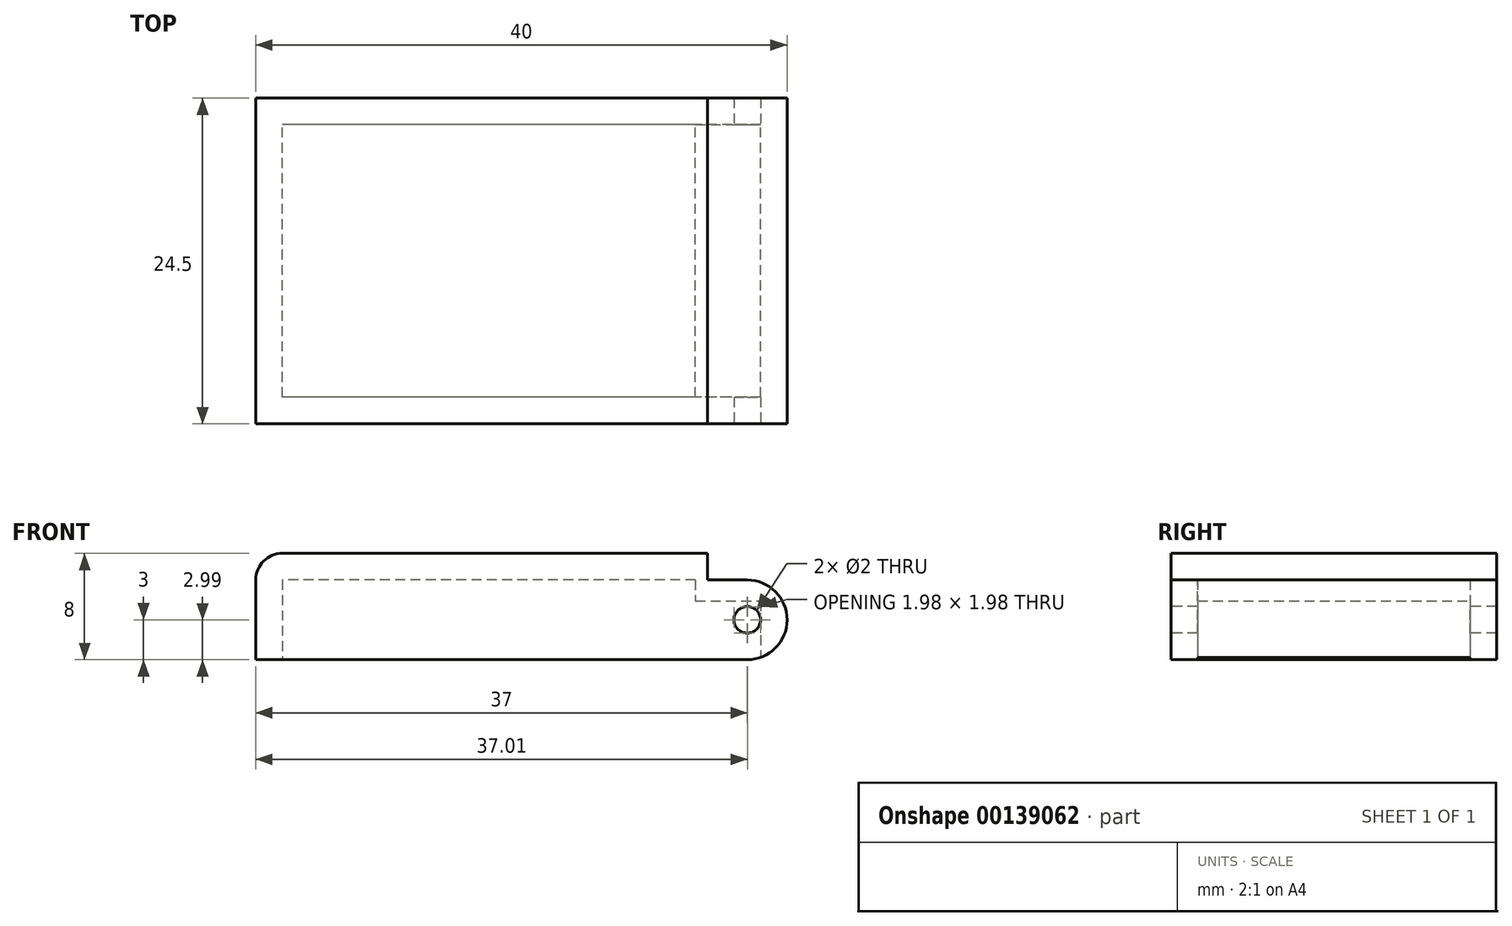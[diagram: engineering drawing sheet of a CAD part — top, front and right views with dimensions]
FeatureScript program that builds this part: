
annotation { "Feature Type Name" : "Feature", "Feature Type Description" : "" }
export const myFeature = defineFeature(function(context is Context, id is Id, definition is map)
    precondition{}
    {
        {
            var Q0;
            Q0=qCreatedBy(makeId("Top.planeOp"),FACE);
            var sketch = newSketch(context, id + "F0", { "sketchPlane" : qUnion([Q0])});
            skLineSegment(sketch, "E0.bottom", {"start": v(20, -12.25) * mm, "end": v(-20, -12.25) * mm});
            skLineSegment(sketch, "E0.top", {"start": v(20, 12.25) * mm, "end": v(-20, 12.25) * mm});
            skLineSegment(sketch, "E0.left", {"start": v(20, -12.25) * mm, "end": v(20, 12.25) * mm});
            skLineSegment(sketch, "E0.right", {"start": v(-20, -12.25) * mm, "end": v(-20, 12.25) * mm});
            skPoint(sketch, "E0.middle", {"position": v(0, 0) * mm});
            skSolve(sketch);
        }
        {
            var Q0;
            Q0 = qSketchRegion(id + "F0", true);
            extrude(context, id + "F1", {"entities" : qUnion([Q0]), "depth" : 8 * mm});
        }
        {
            var Q0;
            Q0=makeQuery(id+"F1.opExtrude","CAP_FACE",FACE,{"disambiguationData":[OSD([sQuery(id+"F0.wireOp",EDGE,"E0.bottom"),sQuery(id+"F0.wireOp",EDGE,"E0.top"),sQuery(id+"F0.wireOp",EDGE,"E0.left"),sQuery(id+"F0.wireOp",EDGE,"E0.right")])],"isStart":true});
            shell(context, id + "F2", {"entities" : qUnion([Q0]), "thickness" : 2 * mm});
        }
        {
            var Q0;
            Q0=makeQuery(id+"F1.opExtrude","SWEPT_FACE",FACE,{"disambiguationData":[OSD([sQuery(id+"F0.wireOp",EDGE,"E0.bottom")])]});
            var sketch = newSketch(context, id + "F3", { "sketchPlane" : qUnion([Q0])});
            skCircle(sketch, "E1", {"center": v(17, 3) * mm, "radius": 1 * mm});
            skArc(sketch, "E2", {"start": v(17, 0) * mm, "mid": v(20, 3) * mm, "end": v(17, 6) * mm});
            skLineSegment(sketch, "E3", {"start": v(17, 3) * mm, "end": v(17, 8) * mm, "construction": true});
            skLineSegment(sketch, "E4", {"start": v(17, 3) * mm, "end": v(0, 3) * mm, "construction": true});
            skLineSegment(sketch, "E5", {"start": v(14, 3) * mm, "end": v(14, 8) * mm, "construction": true});
            skLineSegment(sketch, "E6", {"start": v(17, 6) * mm, "end": v(14, 6) * mm, "construction": true});
            skLineSegment(sketch, "E7", {"start": v(14, 8) * mm, "end": v(14, 6) * mm});
            skLineSegment(sketch, "E8", {"start": v(14, 6) * mm, "end": v(17, 6) * mm});
            skLineSegment(sketch, "E9", {"start": v(17, 0) * mm, "end": v(20, 0) * mm});
            skLineSegment(sketch, "E10", {"start": v(20, 0) * mm, "end": v(20, 3) * mm});
            skLineSegment(sketch, "E11", {"start": v(14, 8) * mm, "end": v(20, 8) * mm});
            skLineSegment(sketch, "E12", {"start": v(20, 8) * mm, "end": v(20, 3) * mm});
            skSolve(sketch);
        }
        {
            var Q0;
            Q0 = qSketchRegion(id + "F3", true);
            extrude(context, id + "F4", {"entities" : qUnion([Q0]), "operationType" : NewBodyOperationType.REMOVE, "oppositeDirection" : true, "depth" : 25 * mm});
        }
        {
            var Q0;
            Q0=makeQuery(id+"F1.opExtrude","CAP_EDGE",EDGE,{"disambiguationData":[OSD([sQuery(id+"F0.wireOp",EDGE,"E0.right")])],"isStart":false});
            var Q1;
            Q1=makeQuery(id+"F4.boolean.opBoolean","COPY",EDGE,{"derivedFrom":makeQuery(id+"F4.opExtrude","SWEPT_EDGE",EDGE,{"disambiguationData":[OSD([sQuery(id+"F0.wireOp",EDGE,"E0.bottom"),sQuery(id+"F3.wireOp",EDGE,"E7"),sQuery(id+"F3.wireOp",EDGE,"E11")])]})});
            fillet(context, id + "F5", {"entities" : qUnion([Q0, Q1]), "radius" : 2 * mm, "tangentPropagation" : true, "allowEdgeOverflow" : false});
        }
        {
            var Q0;
            Q0=makeQuery(id+"F2.opShell","OFFSET_FACE",FACE,{"disambiguationData":[OSD([sQuery(id+"F0.wireOp",EDGE,"E0.top")])]});
            var sketch = newSketch(context, id + "F6", { "sketchPlane" : qUnion([Q0])});
            skLineSegment(sketch, "E13.bottom", {"start": v(13.1, 6) * mm, "end": v(18, 6) * mm});
            skLineSegment(sketch, "E13.top", {"start": v(13.1, 4.41) * mm, "end": v(18, 4.41) * mm});
            skLineSegment(sketch, "E13.left", {"start": v(13.1, 6) * mm, "end": v(13.1, 4.41) * mm});
            skLineSegment(sketch, "E13.right", {"start": v(18, 6) * mm, "end": v(18, 4.41) * mm});
            skSolve(sketch);
        }
        {
            var Q0;
            {var subQ1=sQuery(id+"F6.wireOp",EDGE,"E13.top");Q0=makeQuery(id+"F6.imprint","IMPRINT",FACE,{"disambiguationData":[TD([[makeQuery(id+"F6.imprint","IMPRINT",EDGE,{"derivedFrom":subQ1}),1.0]])]});}
            extrude(context, id + "F7", {"entities" : qUnion([Q0]), "operationType" : NewBodyOperationType.ADD, "depth" : 22.5 * mm});
        }
    });
